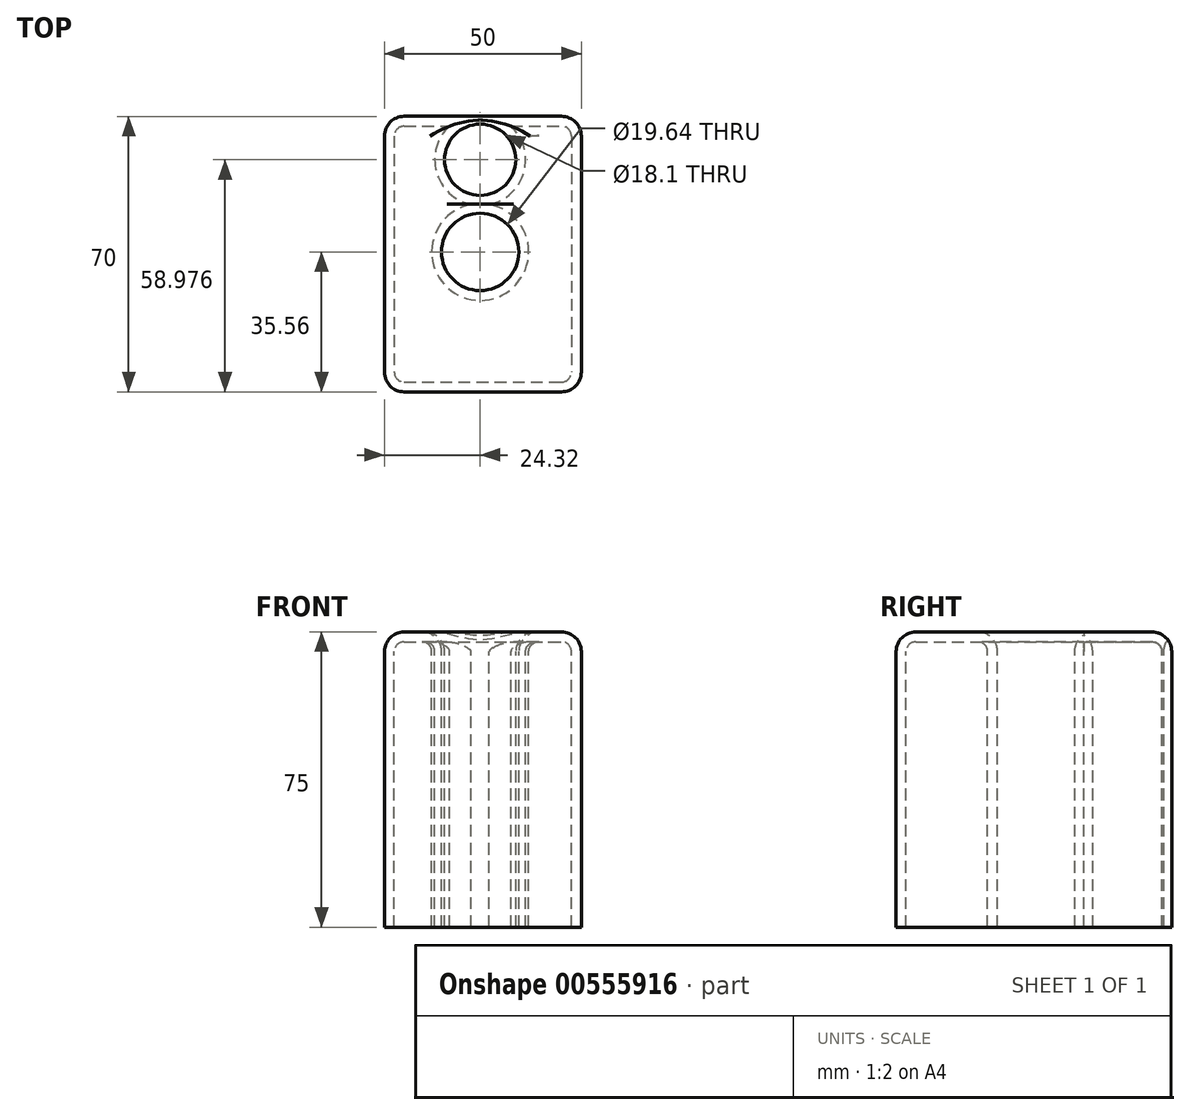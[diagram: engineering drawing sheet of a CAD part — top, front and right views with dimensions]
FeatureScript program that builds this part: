
annotation { "Feature Type Name" : "Feature", "Feature Type Description" : "" }
export const myFeature = defineFeature(function(context is Context, id is Id, definition is map)
    precondition{}
    {
        {
            var Q0;
            Q0=qCreatedBy(makeId("Top.planeOp"),FACE);
            var sketch = newSketch(context, id + "F0", { "sketchPlane" : qUnion([Q0])});
            skLineSegment(sketch, "E0.bottom", {"start": v(-24.32, 34.44) * mm, "end": v(25.68, 34.44) * mm});
            skLineSegment(sketch, "E0.top", {"start": v(-24.32, -35.56) * mm, "end": v(25.68, -35.56) * mm});
            skLineSegment(sketch, "E0.left", {"start": v(-24.32, 34.44) * mm, "end": v(-24.32, -35.56) * mm});
            skLineSegment(sketch, "E0.right", {"start": v(25.68, 34.44) * mm, "end": v(25.68, -35.56) * mm});
            skSolve(sketch);
        }
        {
            var Q0;
            Q0=makeQuery(id+"F0.imprint","IMPRINT",FACE,{"disambiguationData":[TD([[makeQuery(id+"F0.imprint","IMPRINT",EDGE,{"derivedFrom":sQuery(id+"F0.wireOp",EDGE,"E0.bottom")}),-1.0]])]});
            extrude(context, id + "F1", {"entities" : qUnion([Q0]), "depth" : 25 * mm, "offsetDistance" : 25 * mm});
        }
        {
            var Q0;
            Q0=makeQuery(id+"F1.opExtrude","CAP_FACE",FACE,{"disambiguationData":[OSD([sQuery(id+"F0.wireOp",EDGE,"E0.bottom"),sQuery(id+"F0.wireOp",EDGE,"E0.top"),sQuery(id+"F0.wireOp",EDGE,"E0.left"),sQuery(id+"F0.wireOp",EDGE,"E0.right")])],"isStart":false});
            var sketch = newSketch(context, id + "F2", { "sketchPlane" : qUnion([Q0])});
            skCircle(sketch, "E1", {"center": v(0, 0) * mm, "radius": 9.82 * mm});
            skSolve(sketch);
        }
        {
            var Q0;
            Q0=makeQuery(id+"F2.imprint","IMPRINT",FACE,{"disambiguationData":[TD([[makeQuery(id+"F2.imprint","IMPRINT",EDGE,{"derivedFrom":sQuery(id+"F2.wireOp",EDGE,"E1")}),1.0]])]});
            extrude(context, id + "F3", {"entities" : qUnion([Q0]), "operationType" : NewBodyOperationType.REMOVE, "oppositeDirection" : true, "depth" : 25 * mm, "offsetDistance" : 25 * mm});
        }
        {
            var Q0;
            Q0=makeQuery(id+"F1.opExtrude","CAP_FACE",FACE,{"disambiguationData":[OSD([sQuery(id+"F0.wireOp",EDGE,"E0.bottom"),sQuery(id+"F0.wireOp",EDGE,"E0.top"),sQuery(id+"F0.wireOp",EDGE,"E0.left"),sQuery(id+"F0.wireOp",EDGE,"E0.right")])],"isStart":false});
            var sketch = newSketch(context, id + "F4", { "sketchPlane" : qUnion([Q0])});
            skLineSegment(sketch, "E2.bottom", {"start": v(-24.32, -35.56) * mm, "end": v(25.68, -35.56) * mm});
            skLineSegment(sketch, "E2.top", {"start": v(-24.32, 34.44) * mm, "end": v(25.68, 34.44) * mm});
            skLineSegment(sketch, "E2.left", {"start": v(-24.32, -35.56) * mm, "end": v(-24.32, 34.44) * mm});
            skLineSegment(sketch, "E2.right", {"start": v(25.68, -35.56) * mm, "end": v(25.68, 34.44) * mm});
            skSolve(sketch);
        }
        {
            var Q0;
            Q0=makeQuery(id+"F4.imprint","IMPRINT",FACE,{"disambiguationData":[TD([[makeQuery(id+"F4.imprint","IMPRINT",EDGE,{"derivedFrom":sQuery(id+"F4.wireOp",EDGE,"E2.bottom")}),1.0]])]});
            extrude(context, id + "F5", {"entities" : qUnion([Q0]), "operationType" : NewBodyOperationType.ADD, "depth" : 50 * mm, "offsetDistance" : 25 * mm});
        }
        {
            var Q0;
            Q0=makeQuery(id+"F5.opExtrude","CAP_FACE",FACE,{"disambiguationData":[OSD([sQuery(id+"F2.wireOp",EDGE,"E1"),sQuery(id+"F4.wireOp",EDGE,"E2.bottom"),sQuery(id+"F4.wireOp",EDGE,"E2.top"),sQuery(id+"F4.wireOp",EDGE,"E2.left"),sQuery(id+"F4.wireOp",EDGE,"E2.right")])],"isStart":false});
            var sketch = newSketch(context, id + "F6", { "sketchPlane" : qUnion([Q0])});
            skCircle(sketch, "E3", {"center": v(0, 23.42) * mm, "radius": 9.05 * mm});
            skSolve(sketch);
        }
        {
            var Q0;
            Q0=makeQuery(id+"F6.imprint","IMPRINT",FACE,{"disambiguationData":[TD([[makeQuery(id+"F6.imprint","IMPRINT",EDGE,{"derivedFrom":sQuery(id+"F6.wireOp",EDGE,"E3")}),1.0]])]});
            extrude(context, id + "F7", {"entities" : qUnion([Q0]), "operationType" : NewBodyOperationType.REMOVE, "oppositeDirection" : true, "depth" : 75 * mm, "offsetDistance" : 25 * mm});
        }
        {
            var Q0;
            Q0=makeQuery(id+"F5.boolean.opBoolean","MERGE",EDGE,{"derivedFrom":[makeQuery(id+"F1.opExtrude","SWEPT_EDGE",EDGE,{"disambiguationData":[OSD([sQuery(id+"F0.wireOp",EDGE,"E0.top"),sQuery(id+"F0.wireOp",EDGE,"E0.left")])]}),makeQuery(id+"F5.opExtrude","SWEPT_EDGE",EDGE,{"disambiguationData":[OSD([sQuery(id+"F4.wireOp",EDGE,"E2.bottom"),sQuery(id+"F4.wireOp",EDGE,"E2.left")])]})]});
            var Q1;
            Q1=makeQuery(id+"F5.boolean.opBoolean","MERGE",EDGE,{"derivedFrom":[makeQuery(id+"F1.opExtrude","SWEPT_EDGE",EDGE,{"disambiguationData":[OSD([sQuery(id+"F0.wireOp",EDGE,"E0.bottom"),sQuery(id+"F0.wireOp",EDGE,"E0.left")])]}),makeQuery(id+"F5.opExtrude","SWEPT_EDGE",EDGE,{"disambiguationData":[OSD([sQuery(id+"F4.wireOp",EDGE,"E2.top"),sQuery(id+"F4.wireOp",EDGE,"E2.left")])]})]});
            var Q2;
            Q2=makeQuery(id+"F5.boolean.opBoolean","MERGE",EDGE,{"derivedFrom":[makeQuery(id+"F1.opExtrude","SWEPT_EDGE",EDGE,{"disambiguationData":[OSD([sQuery(id+"F0.wireOp",EDGE,"E0.top"),sQuery(id+"F0.wireOp",EDGE,"E0.right")])]}),makeQuery(id+"F5.opExtrude","SWEPT_EDGE",EDGE,{"disambiguationData":[OSD([sQuery(id+"F4.wireOp",EDGE,"E2.bottom"),sQuery(id+"F4.wireOp",EDGE,"E2.right")])]})]});
            var Q3;
            Q3=makeQuery(id+"F5.boolean.opBoolean","MERGE",EDGE,{"derivedFrom":[makeQuery(id+"F1.opExtrude","SWEPT_EDGE",EDGE,{"disambiguationData":[OSD([sQuery(id+"F0.wireOp",EDGE,"E0.bottom"),sQuery(id+"F0.wireOp",EDGE,"E0.right")])]}),makeQuery(id+"F5.opExtrude","SWEPT_EDGE",EDGE,{"disambiguationData":[OSD([sQuery(id+"F4.wireOp",EDGE,"E2.top"),sQuery(id+"F4.wireOp",EDGE,"E2.right")])]})]});
            var Q4;
            Q4=makeQuery(id+"F5.opExtrude","CAP_FACE",FACE,{"disambiguationData":[OSD([sQuery(id+"F2.wireOp",EDGE,"E1"),sQuery(id+"F4.wireOp",EDGE,"E2.bottom"),sQuery(id+"F4.wireOp",EDGE,"E2.top"),sQuery(id+"F4.wireOp",EDGE,"E2.left"),sQuery(id+"F4.wireOp",EDGE,"E2.right")])],"isStart":false});
            var Q5;
            Q5=makeQuery(id+"F5.opExtrude","CAP_EDGE",EDGE,{"disambiguationData":[OSD([sQuery(id+"F4.wireOp",EDGE,"E2.bottom")])],"isStart":false});
            var Q6;
            Q6=makeQuery(id+"F5.opExtrude","CAP_EDGE",EDGE,{"disambiguationData":[OSD([sQuery(id+"F4.wireOp",EDGE,"E2.right")])],"isStart":false});
            var Q7;
            Q7=makeQuery(id+"F5.opExtrude","CAP_EDGE",EDGE,{"disambiguationData":[OSD([sQuery(id+"F4.wireOp",EDGE,"E2.top")])],"isStart":false});
            fillet(context, id + "F8", {"entities" : qUnion([Q0, Q1, Q2, Q3, Q4, Q5, Q6, Q7]), "radius" : 5 * mm, "tangentPropagation" : true, "allowEdgeOverflow" : false});
        }
        {
            var Q0;
            Q0=makeQuery(id+"F1.opExtrude","CAP_FACE",FACE,{"disambiguationData":[OSD([sQuery(id+"F0.wireOp",EDGE,"E0.bottom"),sQuery(id+"F0.wireOp",EDGE,"E0.top"),sQuery(id+"F0.wireOp",EDGE,"E0.left"),sQuery(id+"F0.wireOp",EDGE,"E0.right")])],"isStart":true});
            shell(context, id + "F9", {"entities" : qUnion([Q0]), "thickness" : 2.5 * mm});
        }
    });
